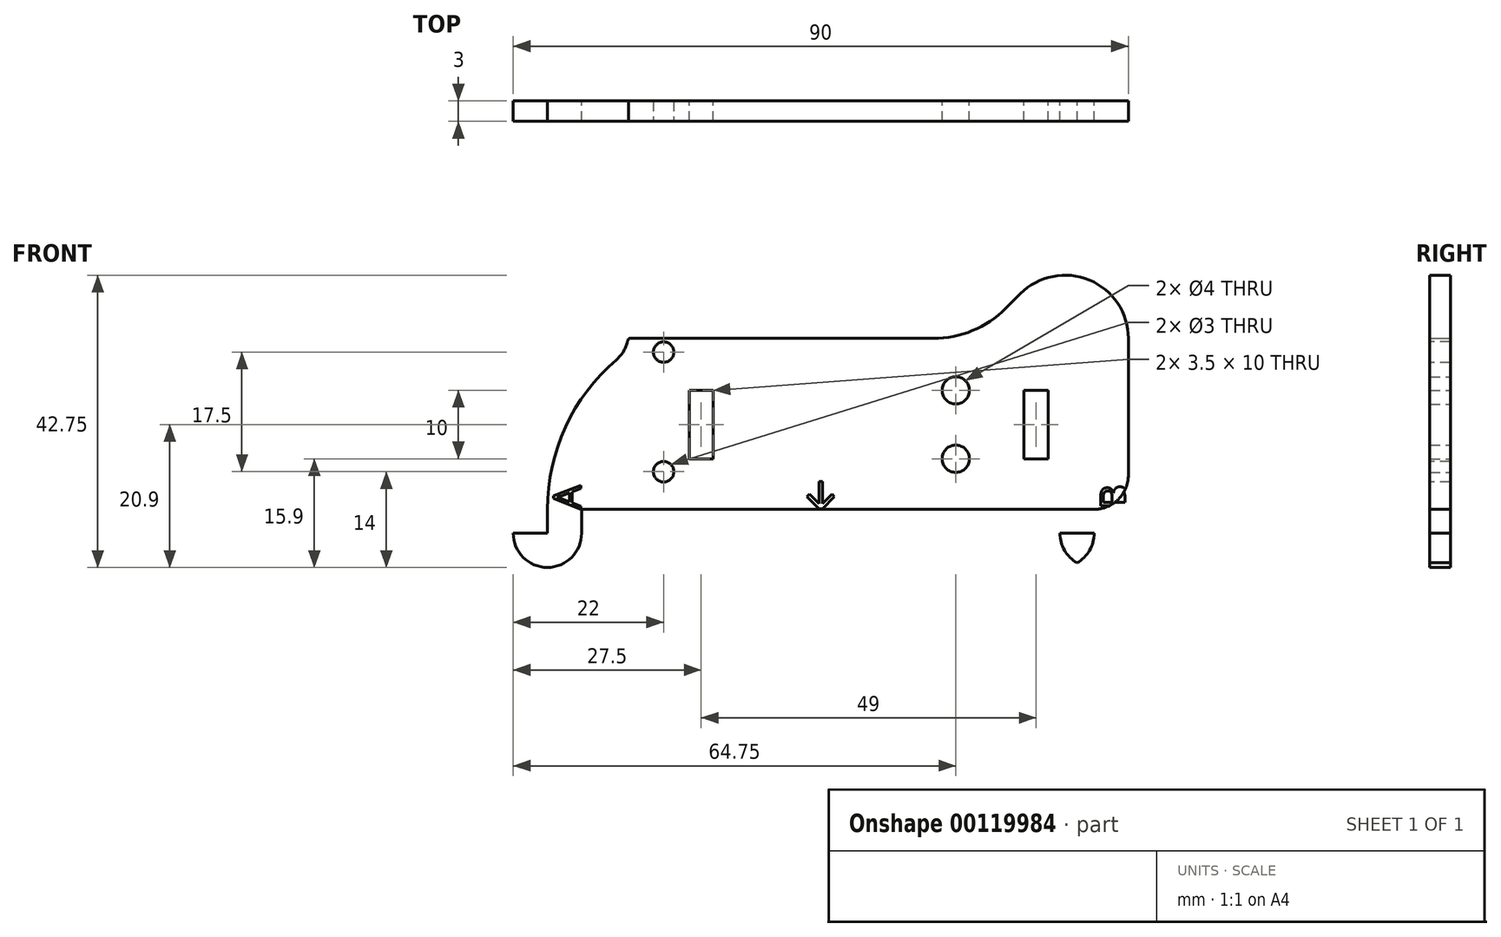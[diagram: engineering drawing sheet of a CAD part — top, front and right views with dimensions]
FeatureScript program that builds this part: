
annotation { "Feature Type Name" : "Feature", "Feature Type Description" : "" }
export const myFeature = defineFeature(function(context is Context, id is Id, definition is map)
    precondition{}
    {
        {
            var Q0;
            Q0=qCreatedBy(makeId("Front.planeOp"),FACE);
            var sketch = newSketch(context, id + "F0", { "sketchPlane" : qUnion([Q0])});
            skLineSegment(sketch, "E0.bottom", {"start": v(0, 0) * mm, "end": v(-80, 0) * mm});
            skLineSegment(sketch, "E0.top", {"start": v(0, 25) * mm, "end": v(-80, 25) * mm});
            skLineSegment(sketch, "E0.left", {"start": v(0, 0) * mm, "end": v(0, 25) * mm});
            skLineSegment(sketch, "E0.right", {"start": v(-80, 0) * mm, "end": v(-80, 25) * mm});
            skArc(sketch, "E1", {"start": v(-75, 25) * mm, "mid": v(-82.4, 13.46) * mm, "end": v(-85, 0) * mm});
            skLineSegment(sketch, "E2", {"start": v(-85, 0) * mm, "end": v(-85, 19.98) * mm, "construction": true});
            skLineSegment(sketch, "E3", {"start": v(-85, 0) * mm, "end": v(-80, 0) * mm});
            skLineSegment(sketch, "E4.top", {"start": v(-85, -8.5) * mm, "end": v(-80, -8.5) * mm});
            skLineSegment(sketch, "E4.left", {"start": v(-85, 0) * mm, "end": v(-85, -8.5) * mm});
            skLineSegment(sketch, "E4.right", {"start": v(-80, 0) * mm, "end": v(-80, -8.5) * mm});
            skLineSegment(sketch, "E5.bottom", {"start": v(-85, -8.5) * mm, "end": v(-90, -8.5) * mm});
            skLineSegment(sketch, "E5.top", {"start": v(-85, -3.5) * mm, "end": v(-90, -3.5) * mm});
            skLineSegment(sketch, "E5.left", {"start": v(-85, -8.5) * mm, "end": v(-85, -3.5) * mm});
            skLineSegment(sketch, "E5.right", {"start": v(-90, -8.5) * mm, "end": v(-90, -3.5) * mm});
            skLineSegment(sketch, "E6.bottom", {"start": v(0, 0) * mm, "end": v(-5, 0) * mm});
            skLineSegment(sketch, "E6.top", {"start": v(0, -8.5) * mm, "end": v(-5, -8.5) * mm});
            skLineSegment(sketch, "E6.left", {"start": v(0, 0) * mm, "end": v(0, -8.5) * mm});
            skLineSegment(sketch, "E6.right", {"start": v(-5, 0) * mm, "end": v(-5, -8.5) * mm});
            skLineSegment(sketch, "E7.bottom", {"start": v(-5, -8.5) * mm, "end": v(-10, -8.5) * mm});
            skLineSegment(sketch, "E7.top", {"start": v(-5, -3.5) * mm, "end": v(-10, -3.5) * mm});
            skLineSegment(sketch, "E7.left", {"start": v(-5, -8.5) * mm, "end": v(-5, -3.5) * mm});
            skLineSegment(sketch, "E7.right", {"start": v(-10, -8.5) * mm, "end": v(-10, -3.5) * mm});
            skArc(sketch, "E8", {"start": v(0, 25) * mm, "mid": v(-5.71, 33.55) * mm, "end": v(-15.8, 31.54) * mm});
            skLineSegment(sketch, "E9", {"start": v(-15.8, 31.54) * mm, "end": v(-22.33, 25) * mm});
            skSolve(sketch);
        }
        {
            var Q0;
            {var subQ6=sQuery(id+"F0.wireOp",EDGE,"E0.bottom");Q0=makeQuery(id+"F0.imprint","IMPRINT",FACE,{"disambiguationData":[TD([[makeQuery(id+"F0.imprint","IMPRINT",EDGE,{"derivedFrom":subQ6}),-1.0]])]});}
            var Q1;
            {var subQ0=sQuery(id+"F0.wireOp",EDGE,"E3");Q1=makeQuery(id+"F0.imprint","IMPRINT",FACE,{"disambiguationData":[TD([[makeQuery(id+"F0.imprint","IMPRINT",EDGE,{"derivedFrom":subQ0}),1.0]])]});}
            var Q2;
            Q2=makeQuery(id+"F0.imprint","IMPRINT",FACE,{"disambiguationData":[TD([[makeQuery(id+"F0.imprint","IMPRINT",EDGE,{"derivedFrom":sQuery(id+"F0.wireOp",EDGE,"E3")}),-1.0]])]});
            var Q3;
            Q3=makeQuery(id+"F0.imprint","IMPRINT",FACE,{"disambiguationData":[TD([[makeQuery(id+"F0.imprint","IMPRINT",EDGE,{"derivedFrom":sQuery(id+"F0.wireOp",EDGE,"E5.bottom")}),-1.0]])]});
            var Q4;
            Q4=makeQuery(id+"F0.imprint","IMPRINT",FACE,{"disambiguationData":[TD([[makeQuery(id+"F0.imprint","IMPRINT",EDGE,{"derivedFrom":sQuery(id+"F0.wireOp",EDGE,"E7.bottom")}),-1.0]])]});
            var Q5;
            Q5=makeQuery(id+"F0.imprint","IMPRINT",FACE,{"disambiguationData":[TD([[makeQuery(id+"F0.imprint","IMPRINT",EDGE,{"derivedFrom":sQuery(id+"F0.wireOp",EDGE,"E6.bottom")}),1.0]])]});
            var Q6;
            {var subQ3=sQuery(id+"F0.wireOp",EDGE,"QHqwsteS-FgLT-0ei4-PVTh-g37n9Dv65TGV");Q6=makeQuery(id+"F0.imprint","IMPRINT",FACE,{"disambiguationData":[TD([[makeQuery(id+"F0.imprint","IMPRINT",EDGE,{"derivedFrom":subQ3}),-1.0]])]});}
            var Q7;
            {var subQ0=sQuery(id+"F0.wireOp",EDGE,"9pQjbTnQ-hIBl-CyJB-6C9K-ikWvvk1ngaaR");Q7=makeQuery(id+"F0.imprint","IMPRINT",FACE,{"disambiguationData":[TD([[makeQuery(id+"F0.imprint","IMPRINT",EDGE,{"derivedFrom":subQ0}),1.0]])]});}
            var Q8;
            {var subQ0=sQuery(id+"F0.wireOp",EDGE,"E8");Q8=makeQuery(id+"F0.imprint","IMPRINT",FACE,{"disambiguationData":[TD([[makeQuery(id+"F0.imprint","IMPRINT",EDGE,{"derivedFrom":subQ0}),1.0]])]});}
            extrude(context, id + "F1", {"entities" : qUnion([Q0, Q1, Q2, Q3, Q4, Q5, Q6, Q7, Q8]), "depth" : 3 * mm});
        }
        {
            var Q0;
            Q0=makeQuery(id+"F1.opExtrude","SWEPT_EDGE",EDGE,{"disambiguationData":[OSD([sQuery(id+"F0.wireOp",EDGE,"E0.top"),sQuery(id+"F0.wireOp",EDGE,"E1")])]});
            var Q1;
            Q1=makeQuery(id+"F1.opExtrude","SWEPT_EDGE",EDGE,{"disambiguationData":[OSD([sQuery(id+"F0.wireOp",EDGE,"E5.bottom"),sQuery(id+"F0.wireOp",EDGE,"E5.right")])]});
            var Q2;
            Q2=makeQuery(id+"F1.opExtrude","SWEPT_EDGE",EDGE,{"disambiguationData":[OSD([sQuery(id+"F0.wireOp",EDGE,"E4.top"),sQuery(id+"F0.wireOp",EDGE,"E4.right")])]});
            var Q3;
            Q3=makeQuery(id+"F1.opExtrude","SWEPT_EDGE",EDGE,{"disambiguationData":[OSD([sQuery(id+"F0.wireOp",EDGE,"E6.top"),sQuery(id+"F0.wireOp",EDGE,"E6.left")])]});
            var Q4;
            Q4=makeQuery(id+"F1.opExtrude","SWEPT_EDGE",EDGE,{"disambiguationData":[OSD([sQuery(id+"F0.wireOp",EDGE,"E7.bottom"),sQuery(id+"F0.wireOp",EDGE,"E7.right")])]});
            var Q5;
            Q5=makeQuery(id+"F1.opExtrude","SWEPT_EDGE",EDGE,{"disambiguationData":[OSD([sQuery(id+"F0.wireOp",EDGE,"cqdcMtzm-qRQj-OcHV-0SQB-a49MjobCelVf"),sQuery(id+"F0.wireOp",EDGE,"QHqwsteS-FgLT-0ei4-PVTh-g37n9Dv65TGV")])]});
            var Q6;
            Q6=makeQuery(id+"F1.opExtrude","SWEPT_EDGE",EDGE,{"disambiguationData":[OSD([sQuery(id+"F0.wireOp",EDGE,"cqdcMtzm-qRQj-OcHV-0SQB-a49MjobCelVf"),sQuery(id+"F0.wireOp",EDGE,"N3RfHHfm-6HXe-rh1R-QiWh-XfKdj2ZUZFwr")])]});
            var Q7;
            Q7=makeQuery(id+"F1.opExtrude","SWEPT_EDGE",EDGE,{"disambiguationData":[OSD([sQuery(id+"F0.wireOp",EDGE,"E0.top"),sQuery(id+"F0.wireOp",EDGE,"E0.left"),sQuery(id+"F0.wireOp",EDGE,"9pQjbTnQ-hIBl-CyJB-6C9K-ikWvvk1ngaaR")])]});
            var Q8;
            Q8=makeQuery(id+"F1.opExtrude","SWEPT_EDGE",EDGE,{"disambiguationData":[OSD([sQuery(id+"F0.wireOp",EDGE,"9pQjbTnQ-hIBl-CyJB-6C9K-ikWvvk1ngaaR"),sQuery(id+"F0.wireOp",EDGE,"E8")])]});
            var Q9;
            Q9=makeQuery(id+"F1.opExtrude","SWEPT_EDGE",EDGE,{"disambiguationData":[OSD([sQuery(id+"F0.wireOp",EDGE,"E8"),sQuery(id+"F0.wireOp",EDGE,"E9")])]});
            fillet(context, id + "F2", {"entities" : qUnion([Q0, Q1, Q2, Q3, Q4, Q5, Q6, Q7, Q8, Q9]), "radius" : 5 * mm, "tangentPropagation" : true, "allowEdgeOverflow" : false});
        }
        {
            var Q0;
            Q0=makeQuery(id+"F1.opExtrude","CAP_FACE",FACE,{"disambiguationData":[OSD([sQuery(id+"F0.wireOp",EDGE,"E0.bottom"),sQuery(id+"F0.wireOp",EDGE,"E0.top"),sQuery(id+"F0.wireOp",EDGE,"E0.left"),sQuery(id+"F0.wireOp",EDGE,"E1"),sQuery(id+"F0.wireOp",EDGE,"E4.top"),sQuery(id+"F0.wireOp",EDGE,"E4.left"),sQuery(id+"F0.wireOp",EDGE,"E4.right"),sQuery(id+"F0.wireOp",EDGE,"E5.bottom"),sQuery(id+"F0.wireOp",EDGE,"E5.top"),sQuery(id+"F0.wireOp",EDGE,"E5.right"),sQuery(id+"F0.wireOp",EDGE,"E6.top"),sQuery(id+"F0.wireOp",EDGE,"E6.left"),sQuery(id+"F0.wireOp",EDGE,"E6.right"),sQuery(id+"F0.wireOp",EDGE,"E7.bottom"),sQuery(id+"F0.wireOp",EDGE,"E7.top"),sQuery(id+"F0.wireOp",EDGE,"E7.right"),sQuery(id+"F0.wireOp",EDGE,"cqdcMtzm-qRQj-OcHV-0SQB-a49MjobCelVf")])],"isStart":true});
            var sketch = newSketch(context, id + "F3", { "sketchPlane" : qUnion([Q0])});
            skLineSegment(sketch, "E10.bottom", {"start": v(15.25, 7.4) * mm, "end": v(11.75, 7.4) * mm});
            skLineSegment(sketch, "E10.top", {"start": v(15.25, 17.4) * mm, "end": v(11.75, 17.4) * mm});
            skLineSegment(sketch, "E10.left", {"start": v(15.25, 7.4) * mm, "end": v(15.25, 17.4) * mm});
            skLineSegment(sketch, "E10.right", {"start": v(11.75, 7.4) * mm, "end": v(11.75, 17.4) * mm});
            skLineSegment(sketch, "E11.bottom", {"start": v(64.25, 7.4) * mm, "end": v(60.75, 7.4) * mm});
            skLineSegment(sketch, "E11.top", {"start": v(64.25, 17.4) * mm, "end": v(60.75, 17.4) * mm});
            skLineSegment(sketch, "E11.left", {"start": v(64.25, 7.4) * mm, "end": v(64.25, 17.4) * mm});
            skLineSegment(sketch, "E11.right", {"start": v(60.75, 7.4) * mm, "end": v(60.75, 17.4) * mm});
            skCircle(sketch, "E12", {"center": v(25.25, 7.4) * mm, "radius": 2 * mm});
            skCircle(sketch, "E13", {"center": v(25.25, 17.4) * mm, "radius": 2 * mm});
            skSolve(sketch);
        }
        {
            var Q0;
            Q0=makeQuery(id+"F3.imprint","IMPRINT",FACE,{"disambiguationData":[TD([[makeQuery(id+"F3.imprint","IMPRINT",EDGE,{"derivedFrom":sQuery(id+"F3.wireOp",EDGE,"E11.bottom")}),-1.0]])]});
            var Q1;
            Q1=makeQuery(id+"F3.imprint","IMPRINT",FACE,{"disambiguationData":[TD([[makeQuery(id+"F3.imprint","IMPRINT",EDGE,{"derivedFrom":sQuery(id+"F3.wireOp",EDGE,"E10.bottom")}),-1.0]])]});
            var Q2;
            Q2=makeQuery(id+"F3.imprint","IMPRINT",FACE,{"disambiguationData":[TD([[makeQuery(id+"F3.imprint","IMPRINT",EDGE,{"derivedFrom":sQuery(id+"F3.wireOp",EDGE,"E12")}),1.0]])]});
            var Q3;
            Q3=makeQuery(id+"F3.imprint","IMPRINT",FACE,{"disambiguationData":[TD([[makeQuery(id+"F3.imprint","IMPRINT",EDGE,{"derivedFrom":sQuery(id+"F3.wireOp",EDGE,"E13")}),1.0]])]});
            extrude(context, id + "F4", {"entities" : qUnion([Q0, Q1, Q2, Q3]), "operationType" : NewBodyOperationType.REMOVE, "oppositeDirection" : true, "depth" : 25 * mm});
        }
        {
            var Q0;
            Q0=makeQuery(id+"F1.opExtrude","CAP_FACE",FACE,{"disambiguationData":[OSD([sQuery(id+"F0.wireOp",EDGE,"E0.bottom"),sQuery(id+"F0.wireOp",EDGE,"E0.top"),sQuery(id+"F0.wireOp",EDGE,"E0.left"),sQuery(id+"F0.wireOp",EDGE,"E1"),sQuery(id+"F0.wireOp",EDGE,"E4.top"),sQuery(id+"F0.wireOp",EDGE,"E4.left"),sQuery(id+"F0.wireOp",EDGE,"E4.right"),sQuery(id+"F0.wireOp",EDGE,"E5.bottom"),sQuery(id+"F0.wireOp",EDGE,"E5.top"),sQuery(id+"F0.wireOp",EDGE,"E5.right"),sQuery(id+"F0.wireOp",EDGE,"E6.top"),sQuery(id+"F0.wireOp",EDGE,"E6.left"),sQuery(id+"F0.wireOp",EDGE,"E6.right"),sQuery(id+"F0.wireOp",EDGE,"E7.bottom"),sQuery(id+"F0.wireOp",EDGE,"E7.top"),sQuery(id+"F0.wireOp",EDGE,"E7.right"),sQuery(id+"F0.wireOp",EDGE,"cqdcMtzm-qRQj-OcHV-0SQB-a49MjobCelVf")])],"isStart":false});
            var sketch = newSketch(context, id + "F5", { "sketchPlane" : qUnion([Q0])});
            skCircle(sketch, "E14", {"center": v(-68, 5.5) * mm, "radius": 1.5 * mm});
            skCircle(sketch, "E15", {"center": v(-68, 23) * mm, "radius": 1.5 * mm});
            skSolve(sketch);
        }
        {
            var Q0;
            Q0=makeQuery(id+"F5.imprint","IMPRINT",FACE,{"disambiguationData":[TD([[makeQuery(id+"F5.imprint","IMPRINT",EDGE,{"derivedFrom":sQuery(id+"F5.wireOp",EDGE,"E15")}),1.0]])]});
            var Q1;
            Q1=makeQuery(id+"F5.imprint","IMPRINT",FACE,{"disambiguationData":[TD([[makeQuery(id+"F5.imprint","IMPRINT",EDGE,{"derivedFrom":sQuery(id+"F5.wireOp",EDGE,"E14")}),1.0]])]});
            extrude(context, id + "F6", {"entities" : qUnion([Q0, Q1]), "operationType" : NewBodyOperationType.REMOVE, "oppositeDirection" : true, "depth" : 25 * mm});
        }
        {
            var Q0;
            Q0=makeQuery(id+"F1.opExtrude","CAP_FACE",FACE,{"disambiguationData":[OSD([sQuery(id+"F0.wireOp",EDGE,"E0.bottom"),sQuery(id+"F0.wireOp",EDGE,"E0.top"),sQuery(id+"F0.wireOp",EDGE,"E0.left"),sQuery(id+"F0.wireOp",EDGE,"E1"),sQuery(id+"F0.wireOp",EDGE,"E4.top"),sQuery(id+"F0.wireOp",EDGE,"E4.left"),sQuery(id+"F0.wireOp",EDGE,"E4.right"),sQuery(id+"F0.wireOp",EDGE,"E5.bottom"),sQuery(id+"F0.wireOp",EDGE,"E5.top"),sQuery(id+"F0.wireOp",EDGE,"E5.right"),sQuery(id+"F0.wireOp",EDGE,"E6.top"),sQuery(id+"F0.wireOp",EDGE,"E6.left"),sQuery(id+"F0.wireOp",EDGE,"E6.right"),sQuery(id+"F0.wireOp",EDGE,"E7.bottom"),sQuery(id+"F0.wireOp",EDGE,"E7.top"),sQuery(id+"F0.wireOp",EDGE,"E7.right"),sQuery(id+"F0.wireOp",EDGE,"cqdcMtzm-qRQj-OcHV-0SQB-a49MjobCelVf")])],"isStart":false});
            var sketch = newSketch(context, id + "F7", { "sketchPlane" : qUnion([Q0])});
            skLineSegment(sketch, "E16", {"start": v(-68, 24.5) * mm, "end": v(-68, 21.5) * mm, "construction": true});
            skLineSegment(sketch, "E17", {"start": v(-69.5, 23) * mm, "end": v(-66.5, 23) * mm, "construction": true});
            skArc(sketch, "E18", {"start": v(-73.5, 23) * mm, "mid": v(-68, 28.5) * mm, "end": v(-62.5, 23) * mm});
            skArc(sketch, "E19", {"start": v(-73.5, 23) * mm, "mid": v(-81.96, 12.86) * mm, "end": v(-85, 0) * mm});
            skArc(sketch, "E20", {"start": v(-62.5, 23) * mm, "mid": v(-42.36, 22.98) * mm, "end": v(-22.33, 25) * mm});
            skSolve(sketch);
        }
        {
            var Q0;
            {var subQ3=sQuery(id+"F7.wireOp",EDGE,"E19");Q0=makeQuery(id+"F7.imprint","IMPRINT",FACE,{"disambiguationData":[TD([[makeQuery(id+"F7.imprint","IMPRINT",EDGE,{"derivedFrom":subQ3}),-1.0]])]});}
            var Q1;
            {var subQ0=sQuery(id+"F7.wireOp",EDGE,"E20");Q1=makeQuery(id+"F7.imprint","IMPRINT",FACE,{"disambiguationData":[TD([[makeQuery(id+"F7.imprint","IMPRINT",EDGE,{"derivedFrom":subQ0}),1.0]])]});}
            extrude(context, id + "F8", {"entities" : qUnion([Q0, Q1]), "operationType" : NewBodyOperationType.REMOVE, "oppositeDirection" : true, "depth" : 25 * mm});
        }
        {
            var Q0;
            Q0 = qSketchRegion(id + "F7", true);
            var Q1;
            {var subQ0=sQuery(id+"F7.wireOp",EDGE,"E18");var subQ2=sQuery(id+"F0.wireOp",EDGE,"E0.top");var subQ5=makeQuery(id+"F1.opExtrude","CAP_EDGE",EDGE,{"disambiguationData":[OSD([subQ2])],"isStart":false});var subQ6=makeQuery(id+"F7.imprint","INTERSECT",VERTEX,{"derivedFrom":[subQ5,subQ0]});Q1=makeQuery(id+"F7.imprint","IMPRINT",FACE,{"disambiguationData":[TD([[makeQuery(id+"F7.imprint","IMPRINT",EDGE,{"disambiguationData":[TD([[subQ6,1.0]])],"derivedFrom":subQ0}),-1.0]])]});}
            extrude(context, id + "F9", {"entities" : qUnion([Q0, Q1]), "oppositeDirection" : true, "depth" : 3 * mm});
        }
        {
            var Q0;
            Q0=makeQuery(id+"F8.boolean.opBoolean","COPY",EDGE,{"derivedFrom":makeQuery(id+"F8.opExtrude","SWEPT_EDGE",EDGE,{"disambiguationData":[OSD([sQuery(id+"F7.wireOp",EDGE,"E18"),sQuery(id+"F7.wireOp",EDGE,"E19")])]})});
            var Q1;
            {var subQ0=sQuery(id+"F0.wireOp",EDGE,"cqdcMtzm-qRQj-OcHV-0SQB-a49MjobCelVf");var subQ1=sQuery(id+"F0.wireOp",EDGE,"E0.top");Q1=makeQuery(id+"F8.boolean.opBoolean","MERGE",EDGE,{"derivedFrom":[makeQuery(id+"F2.opFillet","BLEND_EDGE",EDGE,{"blendedFrom":[makeQuery(id+"F1.opExtrude","SWEPT_EDGE",EDGE,{"disambiguationData":[OSD([subQ1,subQ0])]}),makeQuery(id+"F1.opExtrude","SWEPT_FACE",FACE,{"disambiguationData":[OSD([subQ1])]})],"blendedInto":[makeQuery(id+"F1.opExtrude","SWEPT_FACE",FACE,{"disambiguationData":[OSD([subQ1])]})]}),makeQuery(id+"F8.opExtrude","SWEPT_EDGE",EDGE,{"disambiguationData":[OSD([sQuery(id+"F0.wireOp",EDGE,"E0.bottom"),subQ1,sQuery(id+"F0.wireOp",EDGE,"E0.left"),sQuery(id+"F0.wireOp",EDGE,"E1"),sQuery(id+"F0.wireOp",EDGE,"E4.top"),sQuery(id+"F0.wireOp",EDGE,"E4.left"),sQuery(id+"F0.wireOp",EDGE,"E4.right"),sQuery(id+"F0.wireOp",EDGE,"E5.bottom"),sQuery(id+"F0.wireOp",EDGE,"E5.top"),sQuery(id+"F0.wireOp",EDGE,"E5.right"),sQuery(id+"F0.wireOp",EDGE,"E6.top"),sQuery(id+"F0.wireOp",EDGE,"E6.left"),sQuery(id+"F0.wireOp",EDGE,"E6.right"),sQuery(id+"F0.wireOp",EDGE,"E7.bottom"),sQuery(id+"F0.wireOp",EDGE,"E7.top"),sQuery(id+"F0.wireOp",EDGE,"E7.right"),subQ0,sQuery(id+"F7.wireOp",EDGE,"E20")])]})]});}
            var Q2;
            Q2=makeQuery(id+"F8.boolean.opBoolean","COPY",EDGE,{"derivedFrom":makeQuery(id+"F8.opExtrude","SWEPT_EDGE",EDGE,{"disambiguationData":[OSD([sQuery(id+"F7.wireOp",EDGE,"E18"),sQuery(id+"F7.wireOp",EDGE,"E20")])]})});
            fillet(context, id + "F10", {"entities" : qUnion([Q0, Q1, Q2]), "radius" : 5 * mm, "tangentPropagation" : true, "allowEdgeOverflow" : false});
        }
        {
            var Q0;
            Q0=makeQuery(id+"F1.opExtrude","SWEPT_BODY",BODY,{"disambiguationData":[OSD([sQuery(id+"F0.wireOp",EDGE,"E0.bottom"),sQuery(id+"F0.wireOp",EDGE,"E0.top"),sQuery(id+"F0.wireOp",EDGE,"E0.left"),sQuery(id+"F0.wireOp",EDGE,"E1"),sQuery(id+"F0.wireOp",EDGE,"E4.top"),sQuery(id+"F0.wireOp",EDGE,"E4.left"),sQuery(id+"F0.wireOp",EDGE,"E4.right"),sQuery(id+"F0.wireOp",EDGE,"E5.bottom"),sQuery(id+"F0.wireOp",EDGE,"E5.top"),sQuery(id+"F0.wireOp",EDGE,"E5.right"),sQuery(id+"F0.wireOp",EDGE,"E6.top"),sQuery(id+"F0.wireOp",EDGE,"E6.left"),sQuery(id+"F0.wireOp",EDGE,"E6.right"),sQuery(id+"F0.wireOp",EDGE,"E7.bottom"),sQuery(id+"F0.wireOp",EDGE,"E7.top"),sQuery(id+"F0.wireOp",EDGE,"E7.right"),sQuery(id+"F0.wireOp",EDGE,"cqdcMtzm-qRQj-OcHV-0SQB-a49MjobCelVf")])]});
            var Q1;
            Q1=makeQuery(id+"F9.opExtrude","SWEPT_BODY",BODY,{"disambiguationData":[OSD([sQuery(id+"F0.wireOp",EDGE,"E0.bottom"),sQuery(id+"F0.wireOp",EDGE,"E0.top"),sQuery(id+"F0.wireOp",EDGE,"E0.left"),sQuery(id+"F0.wireOp",EDGE,"E1"),sQuery(id+"F0.wireOp",EDGE,"E4.top"),sQuery(id+"F0.wireOp",EDGE,"E4.left"),sQuery(id+"F0.wireOp",EDGE,"E4.right"),sQuery(id+"F0.wireOp",EDGE,"E5.bottom"),sQuery(id+"F0.wireOp",EDGE,"E5.top"),sQuery(id+"F0.wireOp",EDGE,"E5.right"),sQuery(id+"F0.wireOp",EDGE,"E6.top"),sQuery(id+"F0.wireOp",EDGE,"E6.left"),sQuery(id+"F0.wireOp",EDGE,"E6.right"),sQuery(id+"F0.wireOp",EDGE,"E7.bottom"),sQuery(id+"F0.wireOp",EDGE,"E7.top"),sQuery(id+"F0.wireOp",EDGE,"E7.right"),sQuery(id+"F0.wireOp",EDGE,"cqdcMtzm-qRQj-OcHV-0SQB-a49MjobCelVf"),sQuery(id+"F7.wireOp",EDGE,"E18")])]});
            booleanBodies(context, id + "F11", {"operationType" : BooleanOperationType.UNION, "tools" : qUnion([Q0, Q1])});
        }
        {
            var Q0;
            {var subQ0=sQuery(id+"F0.wireOp",EDGE,"cqdcMtzm-qRQj-OcHV-0SQB-a49MjobCelVf");var subQ1=sQuery(id+"F0.wireOp",EDGE,"E7.right");var subQ2=sQuery(id+"F0.wireOp",EDGE,"E7.top");var subQ3=sQuery(id+"F0.wireOp",EDGE,"E7.bottom");var subQ4=sQuery(id+"F0.wireOp",EDGE,"E6.right");var subQ5=sQuery(id+"F0.wireOp",EDGE,"E6.left");var subQ6=sQuery(id+"F0.wireOp",EDGE,"E6.top");var subQ7=sQuery(id+"F0.wireOp",EDGE,"E5.right");var subQ8=sQuery(id+"F0.wireOp",EDGE,"E5.top");var subQ9=sQuery(id+"F0.wireOp",EDGE,"E5.bottom");var subQ10=sQuery(id+"F0.wireOp",EDGE,"E4.right");var subQ11=sQuery(id+"F0.wireOp",EDGE,"E4.left");var subQ12=sQuery(id+"F0.wireOp",EDGE,"E4.top");var subQ13=sQuery(id+"F0.wireOp",EDGE,"E1");var subQ14=sQuery(id+"F0.wireOp",EDGE,"E0.left");var subQ15=sQuery(id+"F0.wireOp",EDGE,"E0.top");var subQ16=sQuery(id+"F0.wireOp",EDGE,"E0.bottom");Q0=makeQuery(id+"F11.opBoolean","MERGE",FACE,{"derivedFrom":[makeQuery(id+"F9.opExtrude","CAP_FACE",FACE,{"disambiguationData":[OSD([subQ16,subQ15,subQ14,subQ13,subQ12,subQ11,subQ10,subQ9,subQ8,subQ7,subQ6,subQ5,subQ4,subQ3,subQ2,subQ1,subQ0,sQuery(id+"F7.wireOp",EDGE,"E18")])],"isStart":true}),makeQuery(id+"F1.opExtrude","CAP_FACE",FACE,{"disambiguationData":[OSD([subQ16,subQ15,subQ14,subQ13,subQ12,subQ11,subQ10,subQ9,subQ8,subQ7,subQ6,subQ5,subQ4,subQ3,subQ2,subQ1,subQ0])],"isStart":false})]});}
            var sketch = newSketch(context, id + "F12", { "sketchPlane" : qUnion([Q0])});
            skText(sketch, "E21", { "text": "A", "fontName": "OpenSans-Regular.ttf"});
            skText(sketch, "E22", { "text": "B", "fontName": "OpenSans-Regular.ttf"});
            skLineSegment(sketch, "E23.bottom", {"start": v(-47, 0.1) * mm, "end": v(-43, 0.1) * mm, "construction": true});
            skLineSegment(sketch, "E23.top", {"start": v(-47, 4.1) * mm, "end": v(-43, 4.1) * mm, "construction": true});
            skLineSegment(sketch, "E23.left", {"start": v(-47, 0.1) * mm, "end": v(-47, 4.1) * mm, "construction": true});
            skLineSegment(sketch, "E23.right", {"start": v(-43, 0.1) * mm, "end": v(-43, 4.1) * mm, "construction": true});
            skLineSegment(sketch, "E24", {"start": v(-45, 4.1) * mm, "end": v(-45, 7.06) * mm});
            skLineSegment(sketch, "E25.bottom", {"start": v(-45.25, 4.1) * mm, "end": v(-44.75, 4.1) * mm});
            skLineSegment(sketch, "E25.top", {"start": v(-45.25, 0.1) * mm, "end": v(-44.75, 0.1) * mm});
            skLineSegment(sketch, "E25.left", {"start": v(-45.25, 4.1) * mm, "end": v(-45.25, 0.8) * mm});
            skLineSegment(sketch, "E25.right", {"start": v(-44.75, 4.1) * mm, "end": v(-44.75, 0.8) * mm});
            skLineSegment(sketch, "E26", {"start": v(-45.25, 0.1) * mm, "end": v(-47, 1.85) * mm});
            skLineSegment(sketch, "E27", {"start": v(-44.75, 0.1) * mm, "end": v(-43, 1.85) * mm});
            skLineSegment(sketch, "E28", {"start": v(-45.25, 0.8) * mm, "end": v(-47, 2.56) * mm});
            skLineSegment(sketch, "E29", {"start": v(-44.75, 0.8) * mm, "end": v(-43, 2.56) * mm});
            skLineSegment(sketch, "E30", {"start": v(-47, 1.85) * mm, "end": v(-46.65, 2.2) * mm});
            skLineSegment(sketch, "E31", {"start": v(-43, 1.85) * mm, "end": v(-43.35, 2.2) * mm});
            const initialGuessF12  = {"E21": [-0.0801, 0, 0, 1, 0.004], "E22": [-0.0001, 0, 0, 1, 0.004]};
            skSetInitialGuess(sketch, initialGuessF12);
            skSolve(sketch);
        }
        {
            var Q0;
            Q0=makeQuery(id+"F12.imprint","IMPRINT",FACE,{"disambiguationData":[TD([[makeQuery(id+"F12.imprint","IMPRINT",EDGE,{"derivedFrom":sQuery(id+"F12.wireOp",EDGE,"E25.top")}),-1.0]])]});
            var Q1;
            Q1=makeQuery(id+"F12.imprint","IMPRINT",FACE,{"disambiguationData":[TD([[makeQuery(id+"F12.imprint","IMPRINT",EDGE,{"derivedFrom":sQuery(id+"F12.wireOp",EDGE,"E21.sketch_text.stroke-8")}),1.0]])]});
            var Q2;
            Q2=makeQuery(id+"F12.imprint","IMPRINT",FACE,{"disambiguationData":[TD([[makeQuery(id+"F12.imprint","IMPRINT",EDGE,{"derivedFrom":sQuery(id+"F12.wireOp",EDGE,"E22.sketch_text.stroke-18")}),1.0]])]});
            var Q3;
            Q3=makeQuery(id+"F12.imprint","IMPRINT",FACE,{"disambiguationData":[TD([[makeQuery(id+"F12.imprint","IMPRINT",EDGE,{"derivedFrom":sQuery(id+"F12.wireOp",EDGE,"E22.sketch_text.stroke-11")}),1.0]])]});
            extrude(context, id + "F13", {"entities" : qUnion([Q0, Q1, Q2, Q3]), "operationType" : NewBodyOperationType.ADD, "depth" : 0 * mm});
        }
        {
            var Q0;
            Q0=makeQuery(id+"F1.opExtrude","SWEPT_EDGE",EDGE,{"disambiguationData":[OSD([sQuery(id+"F0.wireOp",EDGE,"E0.top"),sQuery(id+"F0.wireOp",EDGE,"cqdcMtzm-qRQj-OcHV-0SQB-a49MjobCelVf"),sQuery(id+"F0.wireOp",EDGE,"QHqwsteS-FgLT-0ei4-PVTh-g37n9Dv65TGV")])]});
            fillet(context, id + "F14", {"entities" : qUnion([Q0]), "radius" : 15 * mm, "tangentPropagation" : true, "allowEdgeOverflow" : false});
        }
    });
